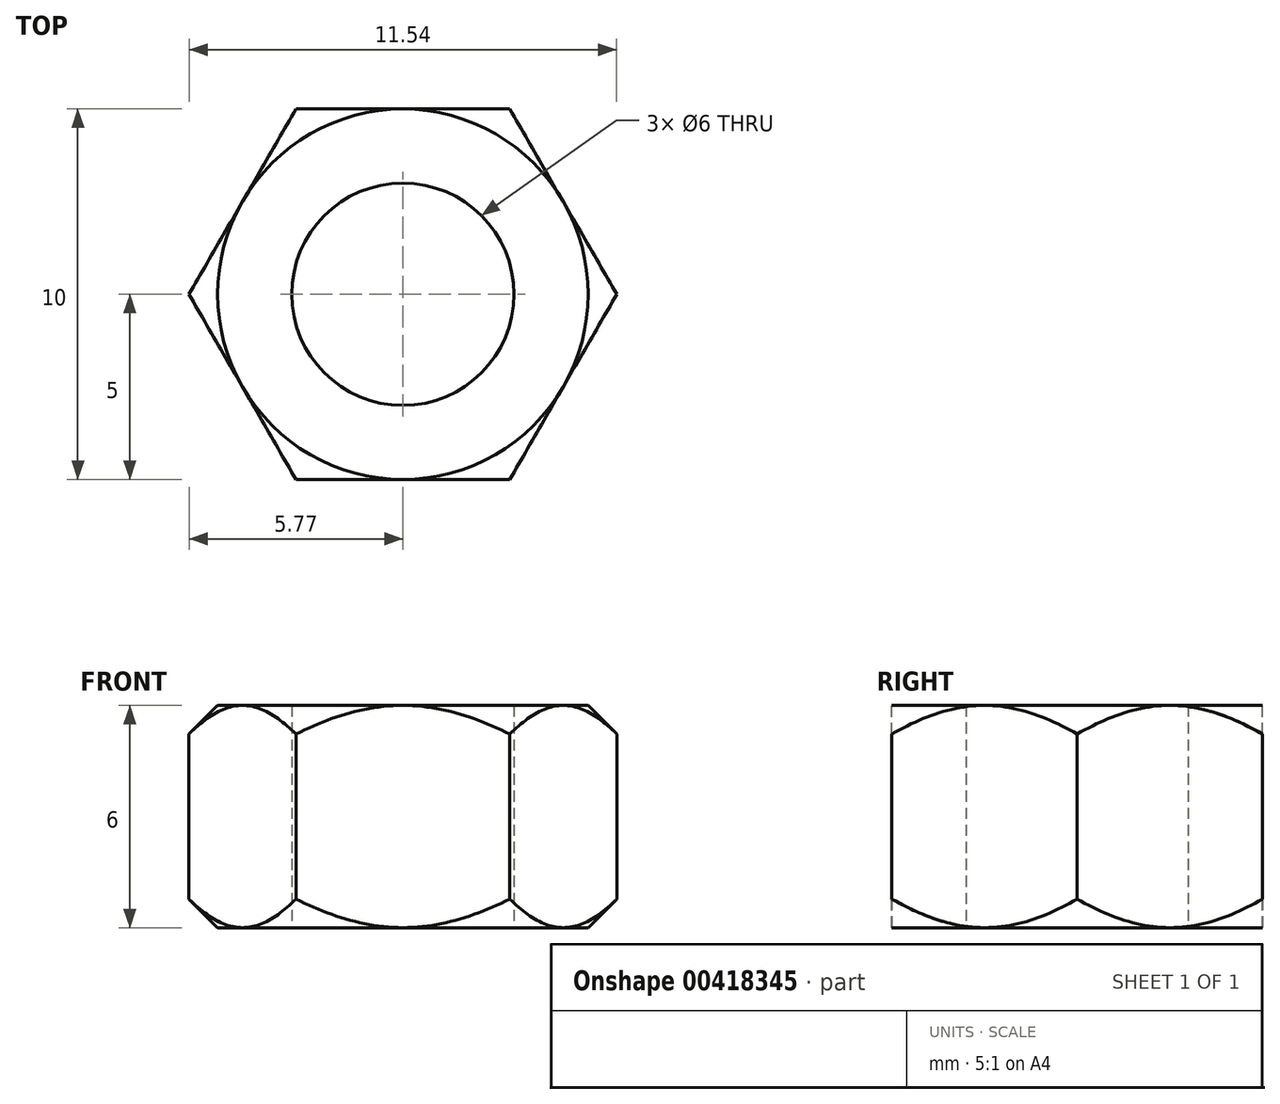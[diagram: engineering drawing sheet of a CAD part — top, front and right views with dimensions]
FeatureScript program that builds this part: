
annotation { "Feature Type Name" : "Feature", "Feature Type Description" : "" }
export const myFeature = defineFeature(function(context is Context, id is Id, definition is map)
    precondition{}
    {
        {
            var Q0;
            Q0=qCreatedBy(makeId("Top.planeOp"),FACE);
            var sketch = newSketch(context, id + "F0", { "sketchPlane" : qUnion([Q0])});
            skCircle(sketch, "E0.cCircle", {"center": v(0, 0) * mm, "radius": 5 * mm, "construction": true});
            skLineSegment(sketch, "E0.0", {"start": v(-2.89, 5) * mm, "end": v(2.89, 5) * mm});
            skLineSegment(sketch, "E0.1", {"start": v(2.89, 5) * mm, "end": v(5.77, 0) * mm});
            skLineSegment(sketch, "E0.2", {"start": v(5.77, 0) * mm, "end": v(2.89, -5) * mm});
            skLineSegment(sketch, "E0.3", {"start": v(2.89, -5) * mm, "end": v(-2.89, -5) * mm});
            skLineSegment(sketch, "E0.4", {"start": v(-2.89, -5) * mm, "end": v(-5.77, 0) * mm});
            skLineSegment(sketch, "E0.5", {"start": v(-5.77, 0) * mm, "end": v(-2.89, 5) * mm});
            skCircle(sketch, "E1", {"center": v(0, 0) * mm, "radius": 3 * mm});
            skCircle(sketch, "E2", {"center": v(0, 0) * mm, "radius": 5.77 * mm});
            skSolve(sketch);
        }
        {
            var Q0;
            Q0=makeQuery(id+"F0.imprint","IMPRINT",FACE,{"disambiguationData":[TD([[makeQuery(id+"F0.imprint","IMPRINT",EDGE,{"derivedFrom":sQuery(id+"F0.wireOp",EDGE,"E0.0")}),-1.0]])]});
            var Q1;
            {var subQ0=sQuery(id+"F0.wireOp",EDGE,"E0.5");Q1=makeQuery(id+"F0.imprint","IMPRINT",FACE,{"disambiguationData":[TD([[makeQuery(id+"F0.imprint","IMPRINT",EDGE,{"derivedFrom":subQ0}),1.0]])]});}
            var Q2;
            {var subQ0=sQuery(id+"F0.wireOp",EDGE,"E0.4");Q2=makeQuery(id+"F0.imprint","IMPRINT",FACE,{"disambiguationData":[TD([[makeQuery(id+"F0.imprint","IMPRINT",EDGE,{"derivedFrom":subQ0}),1.0]])]});}
            var Q3;
            {var subQ0=sQuery(id+"F0.wireOp",EDGE,"E2");var subQ1=sQuery(id+"F0.wireOp",EDGE,"Xk0Y9lW1-gbll-ZgwY-PBr7-DmNMMkUH1pqx");var subQ2=makeQuery(id+"F0.imprint","INTERSECT",VERTEX,{"derivedFrom":[sQuery(id+"F0.wireOp",EDGE,"E0.2"),subQ1,subQ0]});Q3=makeQuery(id+"F0.imprint","IMPRINT",FACE,{"disambiguationData":[TD([[makeQuery(id+"F0.imprint","IMPRINT",EDGE,{"disambiguationData":[TD([[subQ2,1.0]])],"derivedFrom":subQ1}),-1.0]])]});}
            var Q4;
            {var subQ0=sQuery(id+"F0.wireOp",EDGE,"E0.2");Q4=makeQuery(id+"F0.imprint","IMPRINT",FACE,{"disambiguationData":[TD([[makeQuery(id+"F0.imprint","IMPRINT",EDGE,{"derivedFrom":subQ0}),1.0]])]});}
            var Q5;
            {var subQ0=sQuery(id+"F0.wireOp",EDGE,"E0.1");Q5=makeQuery(id+"F0.imprint","IMPRINT",FACE,{"disambiguationData":[TD([[makeQuery(id+"F0.imprint","IMPRINT",EDGE,{"derivedFrom":subQ0}),1.0]])]});}
            var Q6;
            {var subQ0=sQuery(id+"F0.wireOp",EDGE,"E0.0");Q6=makeQuery(id+"F0.imprint","IMPRINT",FACE,{"disambiguationData":[TD([[makeQuery(id+"F0.imprint","IMPRINT",EDGE,{"derivedFrom":subQ0}),1.0]])]});}
            var Q7;
            {var subQ0=sQuery(id+"F0.wireOp",EDGE,"E0.3");Q7=makeQuery(id+"F0.imprint","IMPRINT",FACE,{"disambiguationData":[TD([[makeQuery(id+"F0.imprint","IMPRINT",EDGE,{"derivedFrom":subQ0}),1.0]])]});}
            extrude(context, id + "F1", {"entities" : qUnion([Q0, Q1, Q2, Q3, Q4, Q5, Q6, Q7]), "depth" : 6 * mm});
        }
        {
            var Q0;
            Q0=makeQuery(id+"F1.opExtrude","CAP_EDGE",EDGE,{"disambiguationData":[OSD([sQuery(id+"F0.wireOp",EDGE,"E2")])],"isStart":false});
            var Q1;
            Q1=makeQuery(id+"F1.opExtrude","CAP_EDGE",EDGE,{"disambiguationData":[OSD([sQuery(id+"F0.wireOp",EDGE,"E2")])],"isStart":true});
            chamfer(context, id + "F2", {"entities" : qUnion([Q0, Q1]), "width" : 0.77 * mm, "tangentPropagation" : true});
        }
        {
            var Q0;
            {var subQ0=sQuery(id+"F0.wireOp",EDGE,"E2");var subQ1=sQuery(id+"F0.wireOp",EDGE,"Xk0Y9lW1-gbll-ZgwY-PBr7-DmNMMkUH1pqx");var subQ2=makeQuery(id+"F0.imprint","INTERSECT",VERTEX,{"derivedFrom":[sQuery(id+"F0.wireOp",EDGE,"E0.2"),subQ1,subQ0]});Q0=makeQuery(id+"F0.imprint","IMPRINT",FACE,{"disambiguationData":[TD([[makeQuery(id+"F0.imprint","IMPRINT",EDGE,{"disambiguationData":[TD([[subQ2,1.0]])],"derivedFrom":subQ1}),-1.0]])]});}
            var Q1;
            {var subQ0=sQuery(id+"F0.wireOp",EDGE,"E0.4");Q1=makeQuery(id+"F0.imprint","IMPRINT",FACE,{"disambiguationData":[TD([[makeQuery(id+"F0.imprint","IMPRINT",EDGE,{"derivedFrom":subQ0}),1.0]])]});}
            var Q2;
            {var subQ0=sQuery(id+"F0.wireOp",EDGE,"E0.5");Q2=makeQuery(id+"F0.imprint","IMPRINT",FACE,{"disambiguationData":[TD([[makeQuery(id+"F0.imprint","IMPRINT",EDGE,{"derivedFrom":subQ0}),1.0]])]});}
            var Q3;
            {var subQ0=sQuery(id+"F0.wireOp",EDGE,"E0.0");Q3=makeQuery(id+"F0.imprint","IMPRINT",FACE,{"disambiguationData":[TD([[makeQuery(id+"F0.imprint","IMPRINT",EDGE,{"derivedFrom":subQ0}),1.0]])]});}
            var Q4;
            {var subQ0=sQuery(id+"F0.wireOp",EDGE,"E0.1");Q4=makeQuery(id+"F0.imprint","IMPRINT",FACE,{"disambiguationData":[TD([[makeQuery(id+"F0.imprint","IMPRINT",EDGE,{"derivedFrom":subQ0}),1.0]])]});}
            var Q5;
            {var subQ0=sQuery(id+"F0.wireOp",EDGE,"E0.2");Q5=makeQuery(id+"F0.imprint","IMPRINT",FACE,{"disambiguationData":[TD([[makeQuery(id+"F0.imprint","IMPRINT",EDGE,{"derivedFrom":subQ0}),1.0]])]});}
            var Q6;
            {var subQ0=sQuery(id+"F0.wireOp",EDGE,"E0.3");Q6=makeQuery(id+"F0.imprint","IMPRINT",FACE,{"disambiguationData":[TD([[makeQuery(id+"F0.imprint","IMPRINT",EDGE,{"derivedFrom":subQ0}),1.0]])]});}
            extrude(context, id + "F3", {"entities" : qUnion([Q0, Q1, Q2, Q3, Q4, Q5, Q6]), "operationType" : NewBodyOperationType.REMOVE, "endBound" : BoundingType.THROUGH_ALL, "depth" : 25 * mm});
        }
    });
